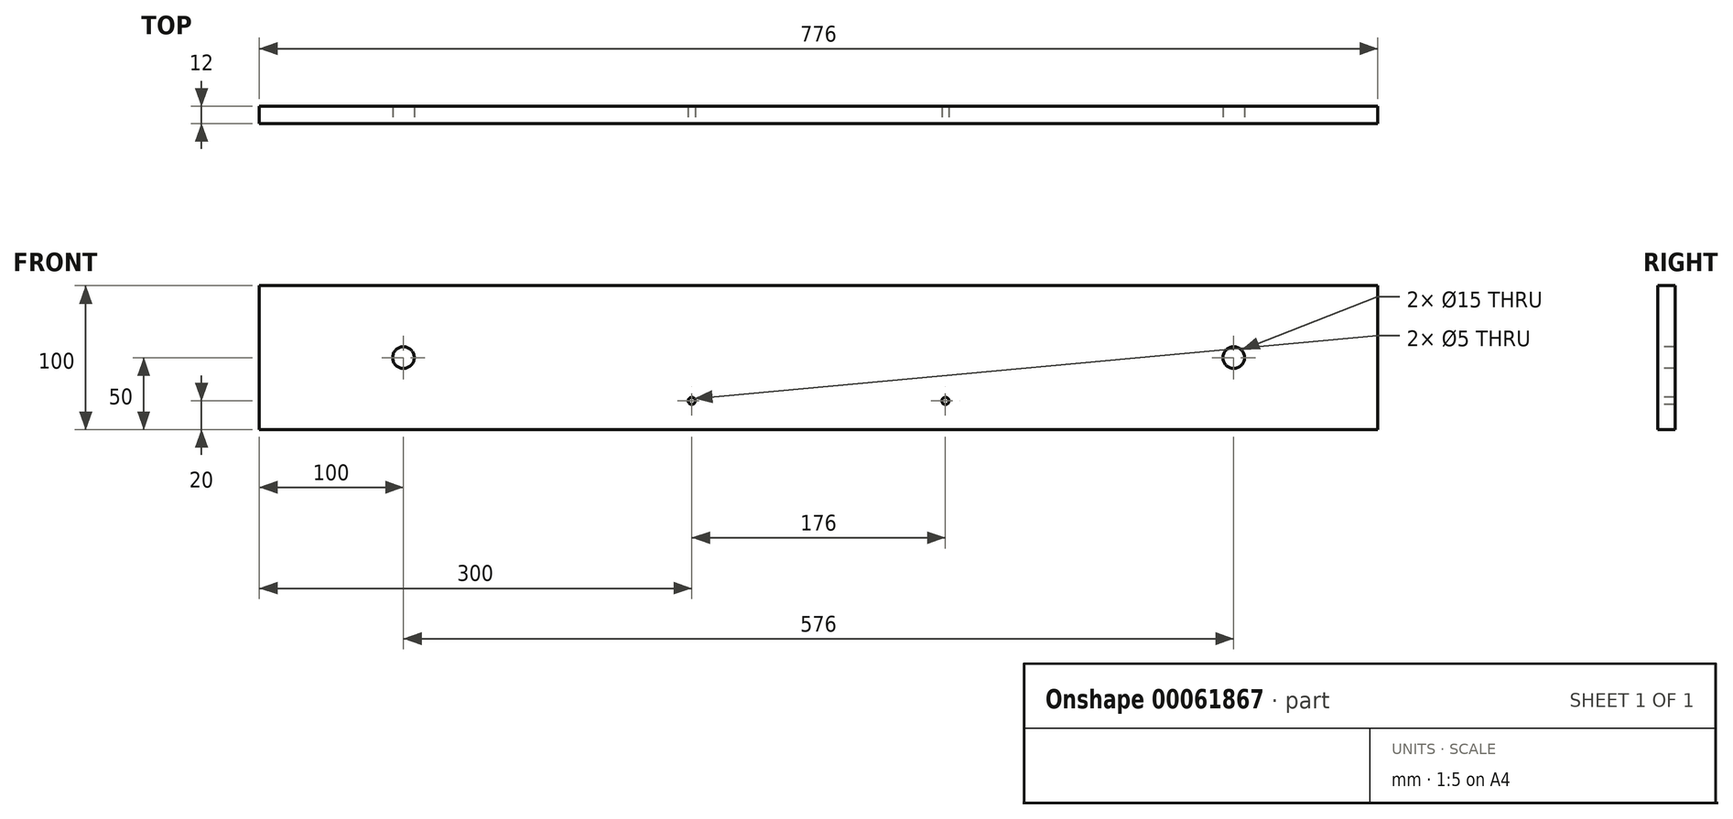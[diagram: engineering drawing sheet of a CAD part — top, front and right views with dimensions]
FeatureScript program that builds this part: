
annotation { "Feature Type Name" : "Feature", "Feature Type Description" : "" }
export const myFeature = defineFeature(function(context is Context, id is Id, definition is map)
    precondition{}
    {
        {
            var Q0;
            Q0=qCreatedBy(makeId("Front.planeOp"),FACE);
            var sketch = newSketch(context, id + "F0", { "sketchPlane" : qUnion([Q0])});
            skLineSegment(sketch, "E0.bottom", {"start": v(0, 0) * mm, "end": v(776, 0) * mm});
            skLineSegment(sketch, "E0.top", {"start": v(0, -100) * mm, "end": v(776, -100) * mm});
            skLineSegment(sketch, "E0.left", {"start": v(0, 0) * mm, "end": v(0, -100) * mm});
            skLineSegment(sketch, "E0.right", {"start": v(776, 0) * mm, "end": v(776, -100) * mm});
            skSolve(sketch);
        }
        {
            var Q0;
            Q0=makeQuery(id+"F0.imprint","IMPRINT",FACE,{"disambiguationData":[TD([[makeQuery(id+"F0.imprint","IMPRINT",EDGE,{"derivedFrom":sQuery(id+"F0.wireOp",EDGE,"E0.bottom")}),-1.0]])]});
            extrude(context, id + "F1", {"entities" : qUnion([Q0]), "oppositeDirection" : true, "depth" : 12 * mm});
        }
        {
            var Q0;
            Q0=makeQuery(id+"F1.opExtrude","CAP_FACE",FACE,{"disambiguationData":[OSD([sQuery(id+"F0.wireOp",EDGE,"E0.bottom"),sQuery(id+"F0.wireOp",EDGE,"E0.top"),sQuery(id+"F0.wireOp",EDGE,"E0.left"),sQuery(id+"F0.wireOp",EDGE,"E0.right")])],"isStart":true});
            var sketch = newSketch(context, id + "F2", { "sketchPlane" : qUnion([Q0])});
            skPoint(sketch, "E1", {"position": v(100, -50) * mm});
            skPoint(sketch, "E2", {"position": v(676, -50) * mm});
            skSolve(sketch);
        }
        {
            var Q0;
            Q0=sQuery(id+"F2.wireOp",VERTEX,"E1");
            var Q1;
            Q1=sQuery(id+"F2.wireOp",VERTEX,"E2");
            var Q2;
            Q2=makeQuery(id+"F1.opExtrude","SWEPT_BODY",BODY,{"disambiguationData":[OSD([sQuery(id+"F0.wireOp",EDGE,"E0.bottom"),sQuery(id+"F0.wireOp",EDGE,"E0.top"),sQuery(id+"F0.wireOp",EDGE,"E0.left"),sQuery(id+"F0.wireOp",EDGE,"E0.right")])]});
            hole(context, id + "F3", {"style" : HoleStyle.SIMPLE, "holeDiameter" : 15 * mm, "endStyle" : HoleEndStyle.THROUGH, "locations" : qUnion([Q0, Q1]), "scope" : qUnion([Q2])});
        }
        {
            var Q0;
            Q0=makeQuery(id+"F1.opExtrude","CAP_FACE",FACE,{"disambiguationData":[OSD([sQuery(id+"F0.wireOp",EDGE,"E0.bottom"),sQuery(id+"F0.wireOp",EDGE,"E0.top"),sQuery(id+"F0.wireOp",EDGE,"E0.left"),sQuery(id+"F0.wireOp",EDGE,"E0.right")])],"isStart":true});
            var sketch = newSketch(context, id + "F4", { "sketchPlane" : qUnion([Q0])});
            skPoint(sketch, "E3", {"position": v(300, -80) * mm});
            skPoint(sketch, "E4", {"position": v(476, -80) * mm});
            skSolve(sketch);
        }
        {
            var Q0;
            Q0=sQuery(id+"F4.wireOp",VERTEX,"E3");
            var Q1;
            Q1=sQuery(id+"F4.wireOp",VERTEX,"E4");
            var Q2;
            Q2=makeQuery(id+"F1.opExtrude","SWEPT_BODY",BODY,{"disambiguationData":[OSD([sQuery(id+"F0.wireOp",EDGE,"E0.bottom"),sQuery(id+"F0.wireOp",EDGE,"E0.top"),sQuery(id+"F0.wireOp",EDGE,"E0.left"),sQuery(id+"F0.wireOp",EDGE,"E0.right")])]});
            hole(context, id + "F5", {"style" : HoleStyle.SIMPLE, "holeDiameter" : 5 * mm, "endStyle" : HoleEndStyle.THROUGH, "locations" : qUnion([Q0, Q1]), "scope" : qUnion([Q2])});
        }
    });
